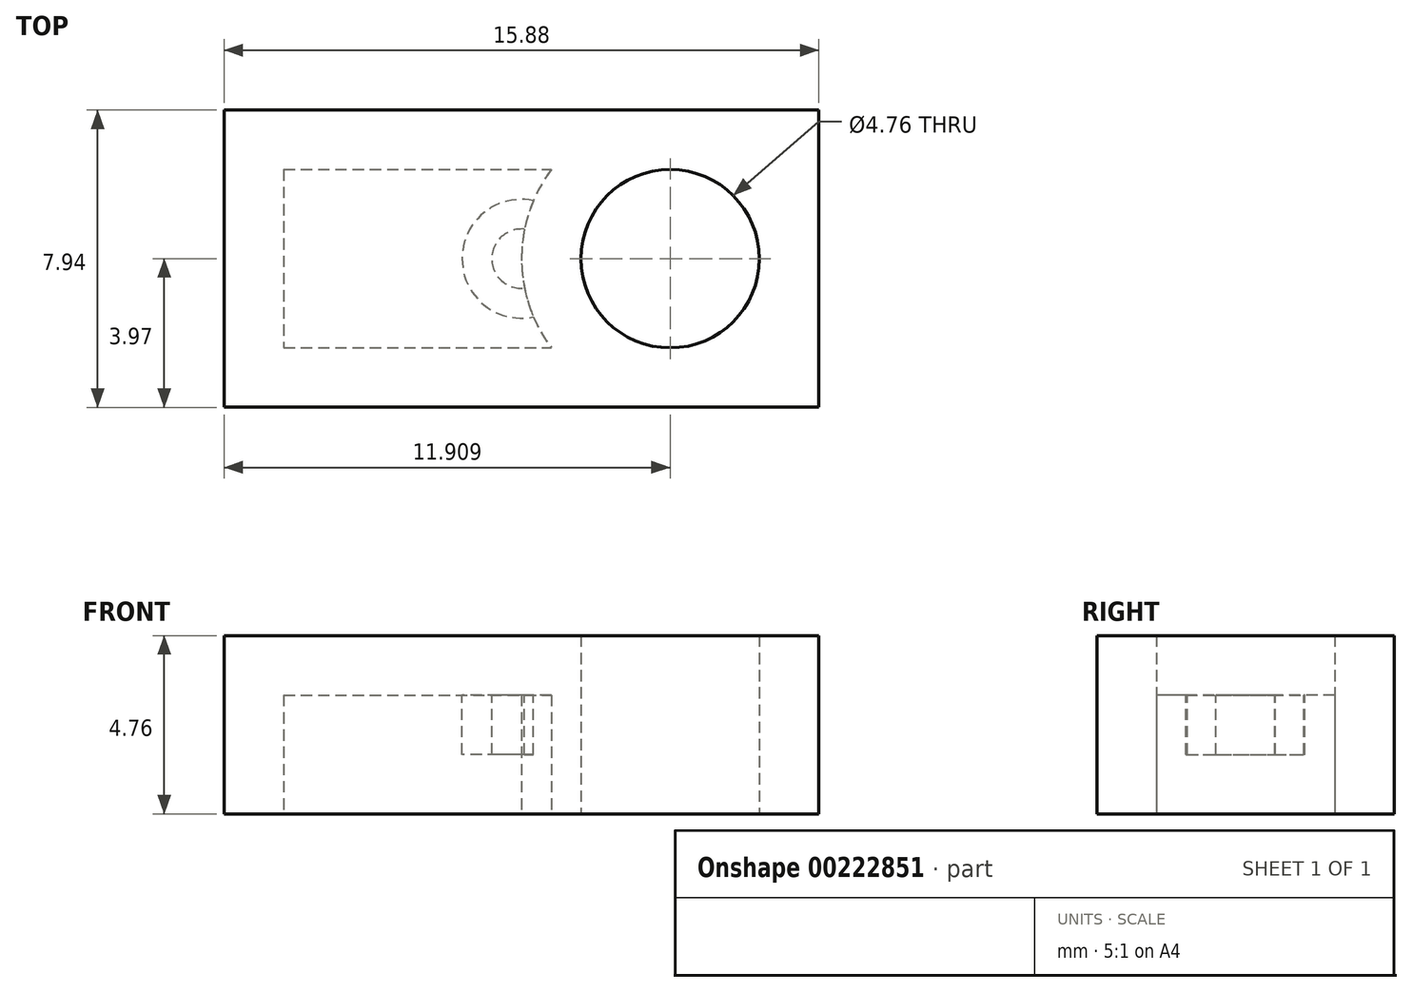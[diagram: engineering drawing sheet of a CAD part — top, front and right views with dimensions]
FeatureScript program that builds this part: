
annotation { "Feature Type Name" : "Feature", "Feature Type Description" : "" }
export const myFeature = defineFeature(function(context is Context, id is Id, definition is map)
    precondition{}
    {
        {
            var Q0;
            Q0=qCreatedBy(makeId("Top.planeOp"),FACE);
            var sketch = newSketch(context, id + "F0", { "sketchPlane" : qUnion([Q0])});
            skLineSegment(sketch, "E0.bottom", {"start": v(-7.94, 3.97) * mm, "end": v(7.94, 3.97) * mm});
            skLineSegment(sketch, "E0.top", {"start": v(-7.94, -3.97) * mm, "end": v(7.94, -3.97) * mm});
            skLineSegment(sketch, "E0.left", {"start": v(-7.94, 3.97) * mm, "end": v(-7.94, -3.97) * mm});
            skLineSegment(sketch, "E0.right", {"start": v(7.94, 3.97) * mm, "end": v(7.94, -3.97) * mm});
            skPoint(sketch, "E0.middle", {"position": v(0, 0) * mm});
            skCircle(sketch, "E1", {"center": v(-3.97, 0) * mm, "radius": 2.38 * mm});
            skCircle(sketch, "E2.MirrorC", {"center": v(3.97, 0) * mm, "radius": 2.38 * mm});
            skSolve(sketch);
        }
        {
            var Q0;
            Q0=makeQuery(id+"F0.imprint","IMPRINT",FACE,{"disambiguationData":[TD([[makeQuery(id+"F0.imprint","IMPRINT",EDGE,{"derivedFrom":sQuery(id+"F0.wireOp",EDGE,"E0.bottom")}),-1.0]])]});
            extrude(context, id + "F1", {"entities" : qUnion([Q0]), "depth" : 3.17 * mm});
        }
        {
            var Q0;
            Q0=makeQuery(id+"F0.imprint","IMPRINT",FACE,{"disambiguationData":[TD([[makeQuery(id+"F0.imprint","IMPRINT",EDGE,{"derivedFrom":sQuery(id+"F0.wireOp",EDGE,"E2.MirrorC")}),-1.0]])]});
            var Q1;
            Q1=makeQuery(id+"F0.imprint","IMPRINT",FACE,{"disambiguationData":[TD([[makeQuery(id+"F0.imprint","IMPRINT",EDGE,{"derivedFrom":sQuery(id+"F0.wireOp",EDGE,"E1")}),1.0]])]});
            extrude(context, id + "F2", {"entities" : qUnion([Q0, Q1]), "operationType" : NewBodyOperationType.ADD, "depth" : 4.76 * mm});
        }
        {
            var Q0;
            {var subQ0=sQuery(id+"F0.wireOp",EDGE,"E2.MirrorC");var subQ1=sQuery(id+"F0.wireOp",EDGE,"E1");Q0=makeQuery(id+"F2.boolean.opBoolean","MERGE",FACE,{"derivedFrom":[makeQuery(id+"F1.opExtrude","CAP_FACE",FACE,{"disambiguationData":[OSD([sQuery(id+"F0.wireOp",EDGE,"E0.bottom"),sQuery(id+"F0.wireOp",EDGE,"E0.top"),sQuery(id+"F0.wireOp",EDGE,"E0.left"),sQuery(id+"F0.wireOp",EDGE,"E0.right"),subQ1,subQ0])],"isStart":true}),makeQuery(id+"F2.opExtrude","CAP_FACE",FACE,{"disambiguationData":[OSD([subQ1])],"isStart":true}),makeQuery(id+"F2.opExtrude","CAP_FACE",FACE,{"disambiguationData":[OSD([subQ0])],"isStart":true})]});}
            shell(context, id + "F3", {"entities" : qUnion([Q0]), "thickness" : 1.59 * mm});
        }
        {
            var Q0;
            Q0=makeQuery(id+"F3.opShell","OFFSET_FACE",FACE,{"disambiguationData":[OSD([sQuery(id+"F0.wireOp",EDGE,"E0.bottom"),sQuery(id+"F0.wireOp",EDGE,"E0.top"),sQuery(id+"F0.wireOp",EDGE,"E0.left"),sQuery(id+"F0.wireOp",EDGE,"E0.right"),sQuery(id+"F0.wireOp",EDGE,"E1"),sQuery(id+"F0.wireOp",EDGE,"E2.MirrorC")])]});
            var sketch = newSketch(context, id + "F4", { "sketchPlane" : qUnion([Q0])});
            skCircle(sketch, "E3", {"center": v(0, 0) * mm, "radius": 1.59 * mm});
            skCircle(sketch, "E4", {"center": v(0, 0) * mm, "radius": 0.8 * mm});
            skSolve(sketch);
        }
        {
            var Q0;
            Q0=makeQuery(id+"F4.imprint","IMPRINT",FACE,{"disambiguationData":[TD([[makeQuery(id+"F4.imprint","IMPRINT",EDGE,{"derivedFrom":sQuery(id+"F4.wireOp",EDGE,"E3")}),1.0]])]});
            extrude(context, id + "F5", {"entities" : qUnion([Q0]), "operationType" : NewBodyOperationType.ADD, "depth" : 1.59 * mm});
        }
    });
